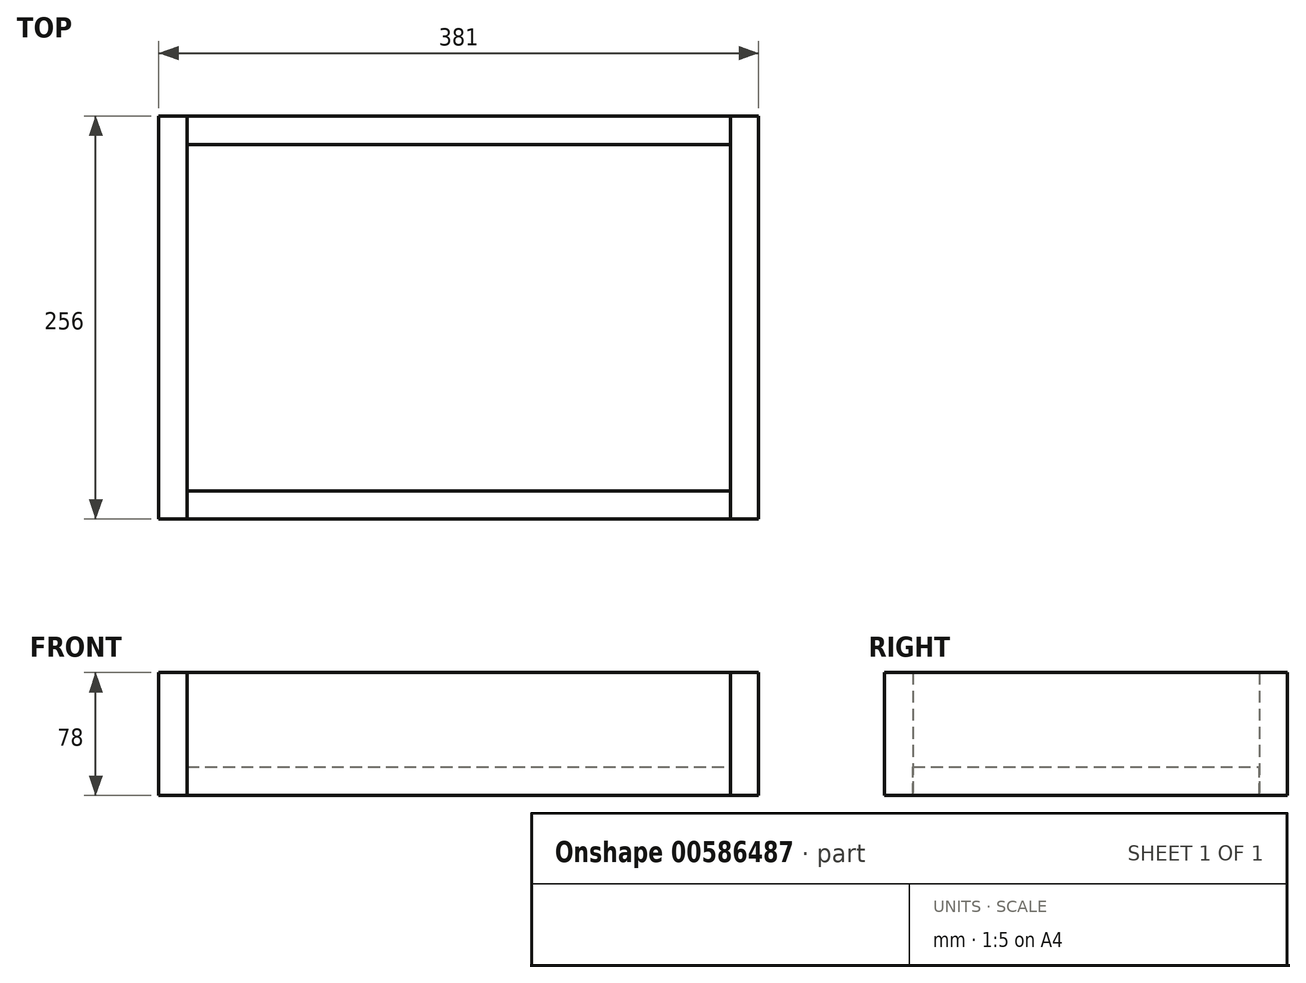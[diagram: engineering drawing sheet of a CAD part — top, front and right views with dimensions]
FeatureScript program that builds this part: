
annotation { "Feature Type Name" : "Feature", "Feature Type Description" : "" }
export const myFeature = defineFeature(function(context is Context, id is Id, definition is map)
    precondition{}
    {
        {
            var Q0;
            Q0=qCreatedBy(makeId("Top.planeOp"),FACE);
            var sketch = newSketch(context, id + "F0", { "sketchPlane" : qUnion([Q0])});
            skLineSegment(sketch, "E0.bottom", {"start": v(-172.5, -110) * mm, "end": v(172.5, -110) * mm});
            skLineSegment(sketch, "E0.top", {"start": v(-172.5, 110) * mm, "end": v(172.5, 110) * mm});
            skLineSegment(sketch, "E0.left", {"start": v(-172.5, -110) * mm, "end": v(-172.5, 110) * mm});
            skLineSegment(sketch, "E0.right", {"start": v(172.5, -110) * mm, "end": v(172.5, 110) * mm});
            skPoint(sketch, "E0.middle", {"position": v(0, 0) * mm});
            skSolve(sketch);
        }
        {
            var Q0;
            Q0 = qSketchRegion(id + "F0", true);
            extrude(context, id + "F1", {"entities" : qUnion([Q0]), "depth" : 60 * mm, "offsetDistance" : 25 * mm});
        }
        {
            var Q0;
            Q0=makeQuery(id+"F1.opExtrude","SWEPT_FACE",FACE,{"disambiguationData":[OSD([sQuery(id+"F0.wireOp",EDGE,"E0.left")])]});
            var sketch = newSketch(context, id + "F2", { "sketchPlane" : qUnion([Q0])});
            skLineSegment(sketch, "E1.bottom", {"start": v(128, -18) * mm, "end": v(-128, -18) * mm});
            skLineSegment(sketch, "E1.top", {"start": v(128, 60) * mm, "end": v(-128, 60) * mm});
            skLineSegment(sketch, "E1.left", {"start": v(128, -18) * mm, "end": v(128, 60) * mm});
            skLineSegment(sketch, "E1.right", {"start": v(-128, -18) * mm, "end": v(-128, 60) * mm});
            skPoint(sketch, "E1.middle", {"position": v(0, 21) * mm});
            skSolve(sketch);
        }
        {
            var Q0;
            Q0 = qSketchRegion(id + "F2", true);
            extrude(context, id + "F3", {"entities" : qUnion([Q0]), "depth" : 18 * mm, "offsetDistance" : 25 * mm});
        }
        {
            var Q0;
            Q0=makeQuery(id+"F1.opExtrude","SWEPT_FACE",FACE,{"disambiguationData":[OSD([sQuery(id+"F0.wireOp",EDGE,"E0.top")])]});
            var sketch = newSketch(context, id + "F4", { "sketchPlane" : qUnion([Q0])});
            skLineSegment(sketch, "E2.bottom", {"start": v(-172.5, 60) * mm, "end": v(172.5, 60) * mm});
            skLineSegment(sketch, "E2.top", {"start": v(-172.5, -18) * mm, "end": v(172.5, -18) * mm});
            skLineSegment(sketch, "E2.left", {"start": v(-172.5, 60) * mm, "end": v(-172.5, -18) * mm});
            skLineSegment(sketch, "E2.right", {"start": v(172.5, 60) * mm, "end": v(172.5, -18) * mm});
            skSolve(sketch);
        }
        {
            var Q0;
            Q0 = qSketchRegion(id + "F4", true);
            extrude(context, id + "F5", {"entities" : qUnion([Q0]), "depth" : 18 * mm, "offsetDistance" : 25 * mm});
        }
        {
            var Q0;
            Q0=makeQuery(id+"F1.opExtrude","CAP_FACE",FACE,{"disambiguationData":[OSD([sQuery(id+"F0.wireOp",EDGE,"E0.bottom"),sQuery(id+"F0.wireOp",EDGE,"E0.top"),sQuery(id+"F0.wireOp",EDGE,"E0.left"),sQuery(id+"F0.wireOp",EDGE,"E0.right")])],"isStart":true});
            var sketch = newSketch(context, id + "F6", { "sketchPlane" : qUnion([Q0])});
            skLineSegment(sketch, "E3.bottom", {"start": v(-172.5, -110) * mm, "end": v(172.5, -110) * mm});
            skLineSegment(sketch, "E3.top", {"start": v(-172.5, 110) * mm, "end": v(172.5, 110) * mm});
            skLineSegment(sketch, "E3.left", {"start": v(-172.5, -110) * mm, "end": v(-172.5, 110) * mm});
            skLineSegment(sketch, "E3.right", {"start": v(172.5, -110) * mm, "end": v(172.5, 110) * mm});
            skSolve(sketch);
        }
        {
            var Q0;
            Q0 = qSketchRegion(id + "F6", true);
            extrude(context, id + "F7", {"entities" : qUnion([Q0]), "depth" : 18 * mm, "offsetDistance" : 25 * mm});
        }
        {
            var Q0;
            Q0=makeQuery(id+"F3.opExtrude","SWEPT_BODY",BODY,{"disambiguationData":[OSD([sQuery(id+"F2.wireOp",EDGE,"E1.bottom"),sQuery(id+"F2.wireOp",EDGE,"E1.top"),sQuery(id+"F2.wireOp",EDGE,"E1.left"),sQuery(id+"F2.wireOp",EDGE,"E1.right")])]});
            var Q1;
            Q1=qCreatedBy(makeId("Right.planeOp"),FACE);
            mirror(context, id + "F8", {"entities" : qUnion([Q0]), "mirrorPlane" : qUnion([Q1])});
        }
        {
            var Q0;
            Q0=makeQuery(id+"F5.opExtrude","SWEPT_BODY",BODY,{"disambiguationData":[OSD([sQuery(id+"F4.wireOp",EDGE,"E2.bottom"),sQuery(id+"F4.wireOp",EDGE,"E2.top"),sQuery(id+"F4.wireOp",EDGE,"E2.left"),sQuery(id+"F4.wireOp",EDGE,"E2.right")])]});
            var Q1;
            Q1=qCreatedBy(makeId("Front.planeOp"),FACE);
            mirror(context, id + "F9", {"entities" : qUnion([Q0]), "mirrorPlane" : qUnion([Q1])});
        }
    });
